# Revit family: QF_ELECTROLUXPROFESSIONAL_1LSNSR_TD6-16_G
name_source: partatom
category: Attrezzature speciali
units: mm (PartAtom-declared; Revit-internal decimal feet)

## family parameters
Basato su piano di lavoro = No
Condiviso = No
Punto di calcolo locali = No
Quota connettore circolare = Usa diametro
Sempre verticale = Sì
Taglio con vuoti quando caricato = No
Tipo di parte = Normale

## types (30) — shared parameters
Depth Actual = 1210 mm  [stored 3.96982 ft]
Height Actual = 1690 mm  [stored 5.54462 ft]
Latent Heat Output = 0.0
Length Actual = 715 mm  [stored 2.3458 ft]
Modello = TD6-16
Produttore = Electrolux Professional
Sensible Heat Output = 0.0
URL = www.electroluxprofessional.com
Watts = 800 W
Weight = 189
zero-valued in all types: Prospetto di default

## per-type parameters (varying)
| type | Cycle | Descrizione | Gas KW | Item Number | Phase | Steam Pounds per Hour | Volts |
| 9872230001 | 50 Hz | TUMBLE DRYER TD6-16 16KG GALVA.DRUM GAS 21KW 230/50/1 COMPASS PRO 6G82 SLVR/SLVR DO.RIGHT REV DISCON DMPR | 21 | 1L0G34 | 1 | 0 | 230 V |
| 9872230021 | 50 Hz | TUMBLE DRYER TD6-16 16KG GALVA.DRUM GAS 21KW 380-415/50/3N COMPASS PRO 6G82 SLVR/SLVR DO.RIGHT REV DMPR | 21 | 1L0G4D | 3 | 0 | 415 V |
| 9872230099 | 60 Hz | TUMBLE DRYER TD6-16 16KG GALVA.DRUM GAS 21KW 220/60/3 COMPASS PRO 6G81 SLVR/SLVR DO.RIGHT REV MB STOP DISCON DMPR | 0 | 1L0H9J | 3 | 0 | 220 V |
| 9872230041 | 50 Hz | TUMBLE DRYER TD6-16 16KG GALVA.DRUM GAS 21KW 380-415/50/3N COMPASS PRO 6L80 2.I/O SLVR/SLVR DO.RIGHT EXT.PM. REV DIS... | 21 | 1LSP7G | 3 | 0 | 415 V |
| 9872230105 | 50 Hz | TUMBLE DRYER TD6-16 16KG GALVA.DRUM GAS 21KW 220/50/1 COMPASS PRO 6A81 SLVR/SLVR DO.RIGHT REV MB STOP DMPR | 0 | 1LT6GM | 1 | 41 | 220 V |
| 9872230100 | 60 Hz | TUMBLE DRYER TD6-16 16KG GALVA.DRUM GAS 21KW 220/60/3 COMPASS PRO 6G82 SLVR/SLVR DO.RIGHT REV STOP DISCON DMPR | 0 | 1L0H9K | 3 | 0 | 220 V |
| 9872230096 | 60 Hz | TUMBLE DRYER TD6-16 16KG SST DRUM GPL 21KW 200/60/3 COMPASS PRO 6G85 SLVR/SLVR DO.RIGHT REV MB DISCON DMPR | 0 | 1LT612 | 3 | 0 | 200 V |
| 9872230016 | 50 Hz | TUMBLE DRYER TD6-16 16KG SST DRUM GAS 21KW 380-415/50/3N COMPASS PRO 6L80 2.I/O SLVR/SLVR DO.RIGHT EXT.PM. REV DISCO... | 21 | 1L0G48 | 3 | 0 | 415 V |
| 9872230006 | 50 Hz | TUMBLE DRYER TD6-16 16KG GALVA.DRUM GAS 21KW 230/50/1 COMPASS PRO 6L80 SLVR/SLVR DO.RIGHT REV DMPR | 21 | 1L0G40 | 1 | 0 | 230 V |
| 9872230093 | 50 Hz | TUMBLE DRYER TD6-16 16KG GALVA.DRUM GPL 21KW 200/50/3 COMPASS PRO 6G85 SLVR/SLVR DO.RIGHT REV MB DISCON DMPR | 0 | 1L0H7R | 3 | 0 | 200 V |
| 9872230026 | 50 Hz | TUMBLE DRYER TD6-16 16KG GALVA.DRUM GAS 21KW 240/50/1 COMPASS PRO 6G81 SLVR/SLVR DO.RIGHT REV MB DISCON DMPR | 21 | 1L0G4J | 1 | 0 | 240 V |
| 9872230083 | 60 Hz | TUMBLE DRYER TD6-16 16KG SST DRUM GPL 21KW 200/60/3 COMPASS PRO 6G86 SLVR/SLVR DO.RIGHT REV DISCON DMPR | 0 | 1LT5Z4 | 3 | 0 | 200 V |
| 9872230013 | 50 Hz | TUMBLE DRYER TD6-16 16KG SST DRUM GAS 21KW 380-415/50/3N COMPASS PRO 6G81 SLVR/SLVR DO.RIGHT REV MB DISCON DMPR | 21 | 1L0G45 | 3 | 0 | 415 V |
| 9872230023 | 50 Hz | TUMBLE DRYER TD6-16 16KG GALVA.DRUM GAS 21KW 380-415/50/3N COMPASS PRO 6G82 SLVR/SLVR DO.RIGHT REV DISCON DMPR | 21 | 1L0G4F | 3 | 0 | 415 V |
| 9872230090 | 50 Hz | TUMBLE DRYER TD6-16 16KG SST DRUM GPL 21KW 200/50/3 COMPASS PRO 6G86 SLVR/SLVR DO.RIGHT REV DISCON DMPR | 0 | 1LT5Z5 | 3 | 0 | 200 V |
| 9872230010 | 50 Hz | TUMBLE DRYER TD6-16 16KG GALVA.DRUM GAS 21KW 240/50/1 COMPASS PRO 6G81 SLVR/SLVR DO.RIGHT REV MB STOP DISCON DMPR | 21 | 1LSP9E | 1 | 0 | 240 V |
| 9872230098 | 60 Hz | TUMBLE DRYER TD6-16 16KG SST DRUM GPL 21KW 200/60/3 COMPASS PRO 6L85 SST/SLVR DO.RIGHT REV DISCON DMPR | 0 | 1L0H93 | 3 | 0 | 200 V |
| 9872230095 | 50 Hz | TUMBLE DRYER TD6-16 16KG SST DRUM GPL 21KW 200/50/3 COMPASS PRO 6G85 SLVR/SLVR DO.RIGHT REV MB DISCON DMPR | 0 | 1LT611 | 3 | 0 | 200 V |
| 9872230025 | 50 Hz | TUMBLE DRYER TD6-16 16KG SST DRUM GAS 21KW 380-415/50/3N COMPASS PRO 6G82 SLVR/SLVR DO.RIGHT REV DISCON DMPR | 21 | 1L0G4H | 3 | 0 | 415 V |
| 9872230055 | 50 Hz | TUMBLE DRYER TD6-16 16KG SST DRUM GAS 21KW 230/50/1 COMPASS PRO 6L80 2.I/O SLVR/SLVR DO.RIGHT EXT.PM. REV DISCON DMPR | 21 | 1LSPCZ | 1 | 0 | 230 V |
| 9872230012 | 50 Hz | TUMBLE DRYER TD6-16 16KG GALVA.DRUM GAS 21KW 230/50/1 COMPASS PRO 6L80 2.I/O SLVR/SLVR DO.RIGHT EXT.PM. REV DISCON DMPR | 21 | 1L0G44 | 1 | 0 | 230 V |
| 9872230097 | 50 Hz | TUMBLE DRYER TD6-16 16KG SST DRUM GPL 21KW 200/50/3 COMPASS PRO 6L85 SST/SLVR DO.RIGHT REV DISCON DMPR | 0 | 1L0H92 | 3 | 0 | 200 V |
| 9872230057 | 50 Hz | TUMBLE DRYER TD6-16 16KG GALVA.DRUM GAS 21KW 240/50/1 COMPASS PRO 6G82 SLVR/SLVR DO.RIGHT REV STOP DISCON DMPR | 21 | 1LA21S | 1 | 0 | 240 V |
| 9872230094 | 50 Hz | TUMBLE DRYER TD6-16 16KG SST DRUM GPL 21KW 200/50/3 COMPASS PRO 6L85 SLVR/SLVR DO.RIGHT REV DISCON DMPR | 0 | 1LT610 | 3 | 0 | 200 V |
| 9872230004 | 50 Hz | TUMBLE DRYER TD6-16 16KG GALVA.DRUM GAS 21KW 230/50/1 COMPASS PRO 6G81 SLVR/SLVR DO.RIGHT REV MB DISCON DMPR | 21 | 1L0G37 | 1 | 0 | 230 V |
| 9872230034 | 50 Hz | TUMBLE DRYER TD6-16 16KG SST DRUM GAS 21KW 220/50/1 COMPASS PRO 6L85 SLVR/SLVR DO.RIGHT REV DMPR | 21 | 1L0G4P | 1 | 0 | 220 V |
| 9872230081 | 50 Hz | TUMBLE DRYER TD6-16 16KG SST DRUM GAS 21KW 230/50/1 COMPASS PRO 6G82 SLVR/SLVR DO.RIGHT REV DISCON DMPR | 0 | 1LSPSH | 1 | 0 | 230 V |
| 9872230091 | 60 Hz | TUMBLE DRYER TD6-16 16KG SST DRUM GPL 21KW 200/60/3 COMPASS PRO 6L85 SLVR/SLVR DO.RIGHT REV DISCON DMPR | 0 | 1LT5Z6 | 3 | 0 | 200 V |
| 9872230044 | 50 Hz | TUMBLE DRYER TD6-16 16KG GALVA.DRUM GAS 21KW 380-415/50/3 COMPASS PRO 6G82 SLVR/SLVR DO.RIGHT REV STOP DISCON DMPR | 21 | 1L0GAT | 3 | 0 | 415 V |
| 9872230011 | 50 Hz | TUMBLE DRYER TD6-16 16KG GALVA.DRUM GAS 21KW 240/50/1 COMPASS PRO 6G81 SLVR/SLVR DO.RIGHT REV MB STOP DISCON DMPR | 21 | 1L0G43 | 1 | 0 | 240 V |

note: [stored X ft] marks values corroborated as IEEE doubles in the binary element streams (Revit-internal decimal feet)

## geometry (parser evidence)
native form markers: Blend x8
no freeform markers — native parametric forms only
